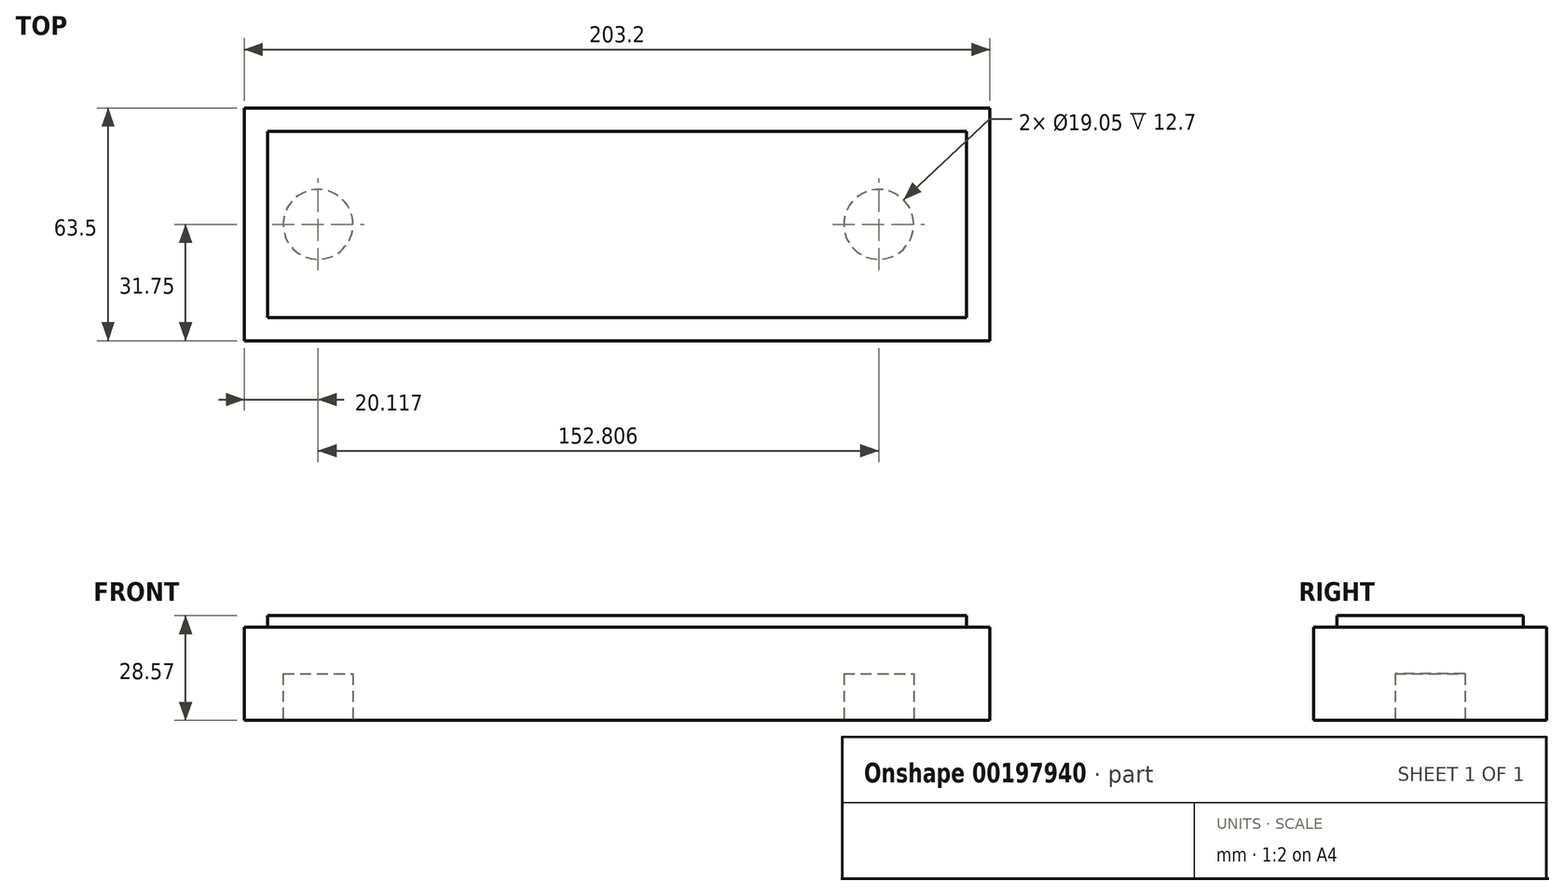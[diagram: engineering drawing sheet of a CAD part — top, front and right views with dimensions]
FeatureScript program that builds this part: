
annotation { "Feature Type Name" : "Feature", "Feature Type Description" : "" }
export const myFeature = defineFeature(function(context is Context, id is Id, definition is map)
    precondition{}
    {
        {
            var Q0;
            Q0=qCreatedBy(makeId("Top.planeOp"),FACE);
            var sketch = newSketch(context, id + "F0", { "sketchPlane" : qUnion([Q0])});
            skLineSegment(sketch, "E0.bottom", {"start": v(101.6, -31.75) * mm, "end": v(-101.6, -31.75) * mm});
            skLineSegment(sketch, "E0.top", {"start": v(101.6, 31.75) * mm, "end": v(-101.6, 31.75) * mm});
            skLineSegment(sketch, "E0.left", {"start": v(101.6, -31.75) * mm, "end": v(101.6, 31.75) * mm});
            skLineSegment(sketch, "E0.right", {"start": v(-101.6, -31.75) * mm, "end": v(-101.6, 31.75) * mm});
            skPoint(sketch, "E0.middle", {"position": v(0, 0) * mm});
            skSolve(sketch);
        }
        {
            var Q0;
            Q0=makeQuery(id+"F0.imprint","IMPRINT",FACE,{"disambiguationData":[TD([[makeQuery(id+"F0.imprint","IMPRINT",EDGE,{"derivedFrom":sQuery(id+"F0.wireOp",EDGE,"E0.bottom")}),-1.0]])]});
            extrude(context, id + "F1", {"entities" : qUnion([Q0]), "depth" : 25.4 * mm});
        }
        {
            var Q0;
            Q0=makeQuery(id+"F1.opExtrude","CAP_FACE",FACE,{"disambiguationData":[OSD([sQuery(id+"F0.wireOp",EDGE,"E0.bottom"),sQuery(id+"F0.wireOp",EDGE,"E0.top"),sQuery(id+"F0.wireOp",EDGE,"E0.left"),sQuery(id+"F0.wireOp",EDGE,"E0.right")])],"isStart":true});
            var sketch = newSketch(context, id + "F2", { "sketchPlane" : qUnion([Q0])});
            skPoint(sketch, "E1.endSnap0", {"position": v(-101.6, 0) * mm});
            skPoint(sketch, "E2.endSnap0", {"position": v(101.6, 0) * mm});
            skLineSegment(sketch, "E3", {"start": v(101.6, 0) * mm, "end": v(80.85, 0) * mm});
            skLineSegment(sketch, "E4", {"start": v(80.85, 0) * mm, "end": v(71.32, 0) * mm});
            skCircle(sketch, "E5", {"center": v(-81.48, 0) * mm, "radius": 9.53 * mm});
            skCircle(sketch, "E6", {"center": v(71.32, 0) * mm, "radius": 9.53 * mm});
            skSolve(sketch);
        }
        {
            var Q0;
            Q0 = qSketchRegion(id + "F2", true);
            extrude(context, id + "F3", {"entities" : qUnion([Q0]), "operationType" : NewBodyOperationType.REMOVE, "oppositeDirection" : true, "depth" : 12.7 * mm});
        }
        {
            var Q0;
            Q0=makeQuery(id+"F1.opExtrude","CAP_FACE",FACE,{"disambiguationData":[OSD([sQuery(id+"F0.wireOp",EDGE,"E0.bottom"),sQuery(id+"F0.wireOp",EDGE,"E0.top"),sQuery(id+"F0.wireOp",EDGE,"E0.left"),sQuery(id+"F0.wireOp",EDGE,"E0.right")])],"isStart":false});
            var sketch = newSketch(context, id + "F4", { "sketchPlane" : qUnion([Q0])});
            skLineSegment(sketch, "E7.bottom", {"start": v(95.25, -25.4) * mm, "end": v(-95.25, -25.4) * mm});
            skLineSegment(sketch, "E7.top", {"start": v(95.25, 25.4) * mm, "end": v(-95.25, 25.4) * mm});
            skLineSegment(sketch, "E7.left", {"start": v(95.25, -25.4) * mm, "end": v(95.25, 25.4) * mm});
            skLineSegment(sketch, "E7.right", {"start": v(-95.25, -25.4) * mm, "end": v(-95.25, 25.4) * mm});
            skPoint(sketch, "E7.middle", {"position": v(0, 0) * mm});
            skSolve(sketch);
        }
        {
            var Q0;
            Q0 = qSketchRegion(id + "F4", true);
            extrude(context, id + "F5", {"entities" : qUnion([Q0]), "operationType" : NewBodyOperationType.ADD, "depth" : 3.17 * mm});
        }
    });
